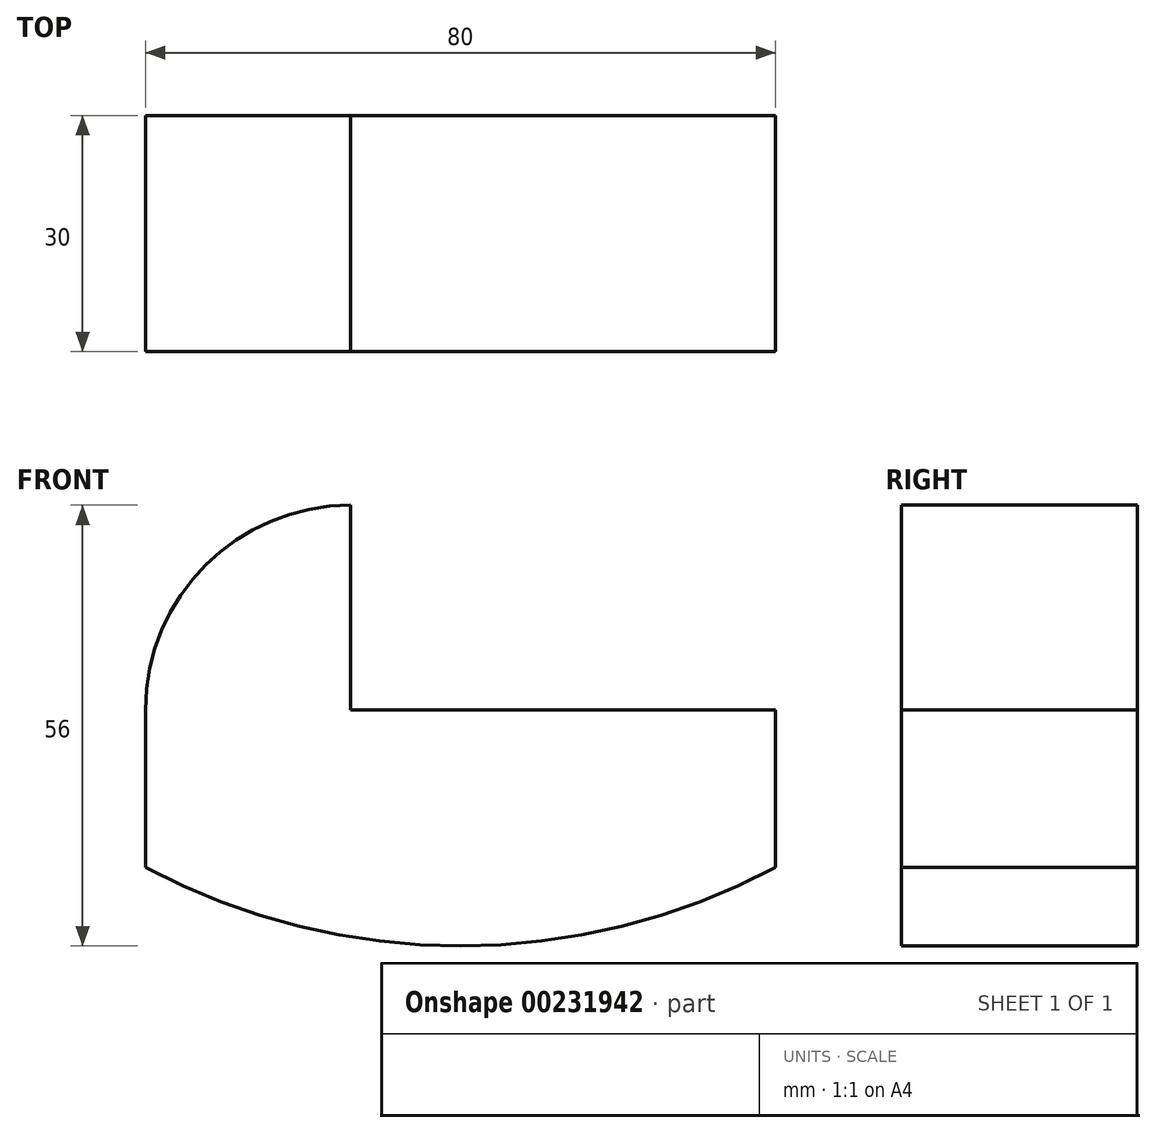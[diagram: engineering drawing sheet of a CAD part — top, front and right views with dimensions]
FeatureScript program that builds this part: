
annotation { "Feature Type Name" : "Feature", "Feature Type Description" : "" }
export const myFeature = defineFeature(function(context is Context, id is Id, definition is map)
    precondition{}
    {
        {
            var Q0;
            Q0=qCreatedBy(makeId("Front.planeOp"),FACE);
            var sketch = newSketch(context, id + "F0", { "sketchPlane" : qUnion([Q0])});
            skLineSegment(sketch, "E0", {"start": v(-54, 46.12) * mm, "end": v(-54, 20) * mm});
            skLineSegment(sketch, "E1", {"start": v(-54, 20) * mm, "end": v(0, 20) * mm});
            skLineSegment(sketch, "E2", {"start": v(0, 20) * mm, "end": v(0, 0) * mm});
            skArc(sketch, "E3", {"start": v(-80, 20) * mm, "mid": v(-72.38, 38.38) * mm, "end": v(-54, 46) * mm});
            skLineSegment(sketch, "E4", {"start": v(-80, 20) * mm, "end": v(-80, 0) * mm});
            skArc(sketch, "E5", {"start": v(-80, 0) * mm, "mid": v(-40, -10) * mm, "end": v(0, 0) * mm});
            skSolve(sketch);
        }
        {
            var Q0;
            {var subQ1=sQuery(id+"F0.wireOp",EDGE,"E1");Q0=makeQuery(id+"F0.imprint","IMPRINT",FACE,{"disambiguationData":[TD([[makeQuery(id+"F0.imprint","IMPRINT",EDGE,{"derivedFrom":subQ1}),-1.0]])]});}
            extrude(context, id + "F1", {"entities" : qUnion([Q0]), "depth" : 30 * mm});
        }
    });
